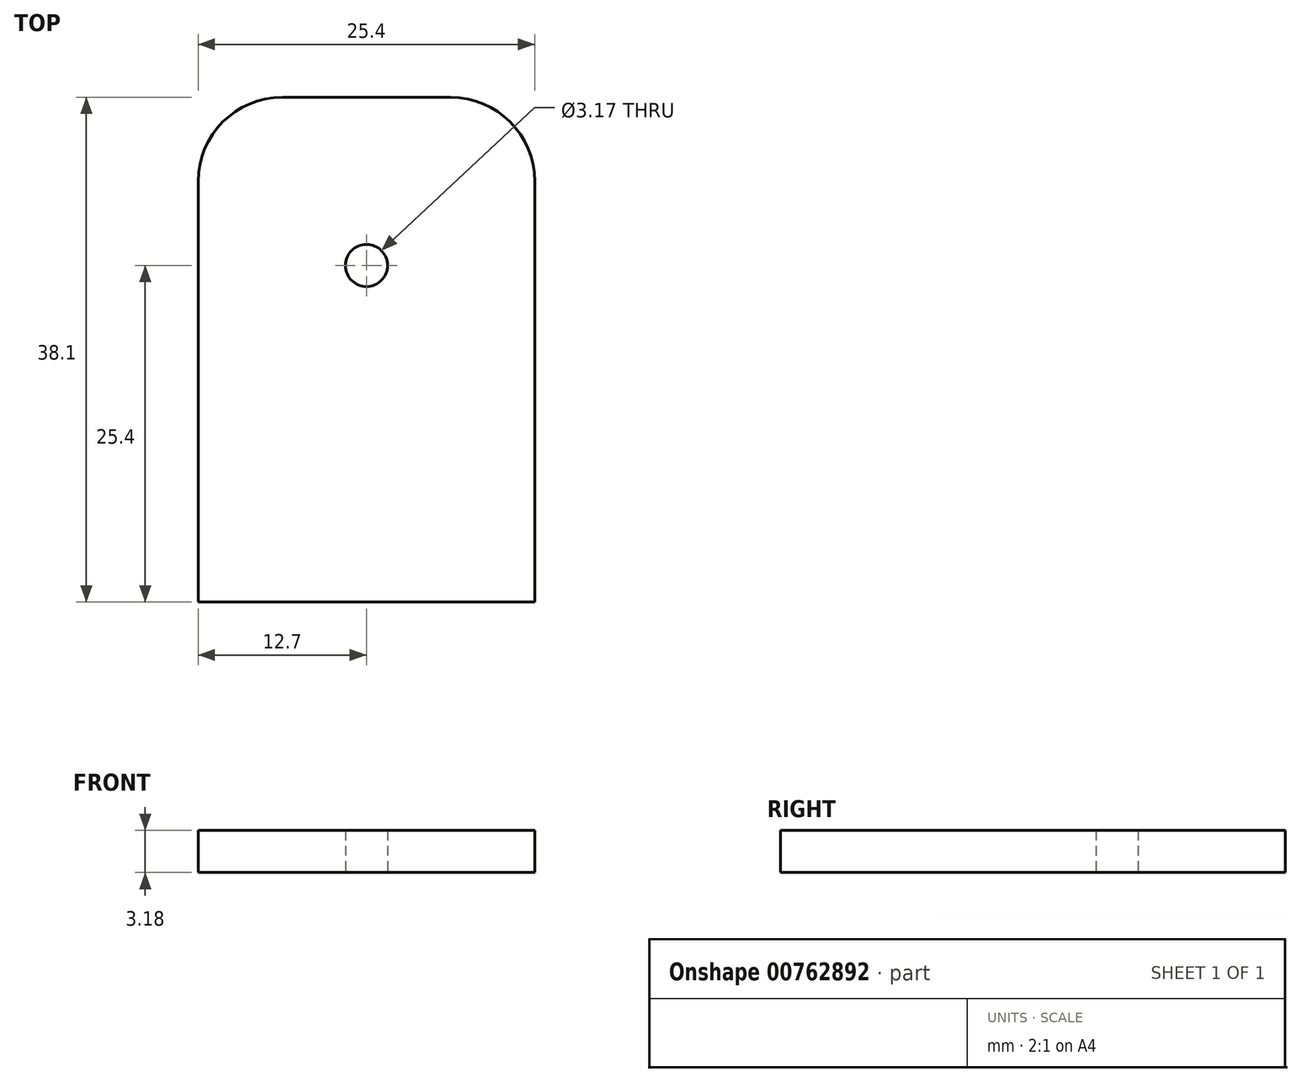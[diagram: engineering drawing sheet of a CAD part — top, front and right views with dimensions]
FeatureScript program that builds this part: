
annotation { "Feature Type Name" : "Feature", "Feature Type Description" : "" }
export const myFeature = defineFeature(function(context is Context, id is Id, definition is map)
    precondition{}
    {
        {
            var Q0;
            Q0=qCreatedBy(makeId("Top.planeOp"),FACE);
            var sketch = newSketch(context, id + "F0", { "sketchPlane" : qUnion([Q0])});
            skLineSegment(sketch, "E0.bottom", {"start": v(6.35, 0) * mm, "end": v(19.05, 0) * mm});
            skLineSegment(sketch, "E0.top", {"start": v(0, -38.1) * mm, "end": v(25.4, -38.1) * mm});
            skLineSegment(sketch, "E0.left", {"start": v(0, -6.35) * mm, "end": v(0, -38.1) * mm});
            skLineSegment(sketch, "E0.right", {"start": v(25.4, -6.35) * mm, "end": v(25.4, -38.1) * mm});
            skCircle(sketch, "E1", {"center": v(12.7, -12.7) * mm, "radius": 1.59 * mm});
            skPoint(sketch, "E1.centerSnap0", {"position": v(12.7, 0) * mm});
            skPoint(sketch, "E2.visualSharp", {"position": v(0, 0) * mm});
            skArc(sketch, "E2.filletArc", {"start": v(6.35, 0) * mm, "mid": v(1.86, -1.86) * mm, "end": v(0, -6.35) * mm});
            skPoint(sketch, "E3.visualSharp", {"position": v(25.4, 0) * mm});
            skArc(sketch, "E3.filletArc", {"start": v(25.4, -6.35) * mm, "mid": v(23.54, -1.86) * mm, "end": v(19.05, 0) * mm});
            skSolve(sketch);
        }
        {
            var Q0;
            Q0=makeQuery(id+"F0.imprint","IMPRINT",FACE,{"disambiguationData":[TD([[makeQuery(id+"F0.imprint","IMPRINT",EDGE,{"derivedFrom":sQuery(id+"F0.wireOp",EDGE,"E0.bottom")}),-1.0]])]});
            extrude(context, id + "F1", {"entities" : qUnion([Q0]), "depth" : 3.17 * mm, "offsetDistance" : 25.4 * mm});
        }
    });
